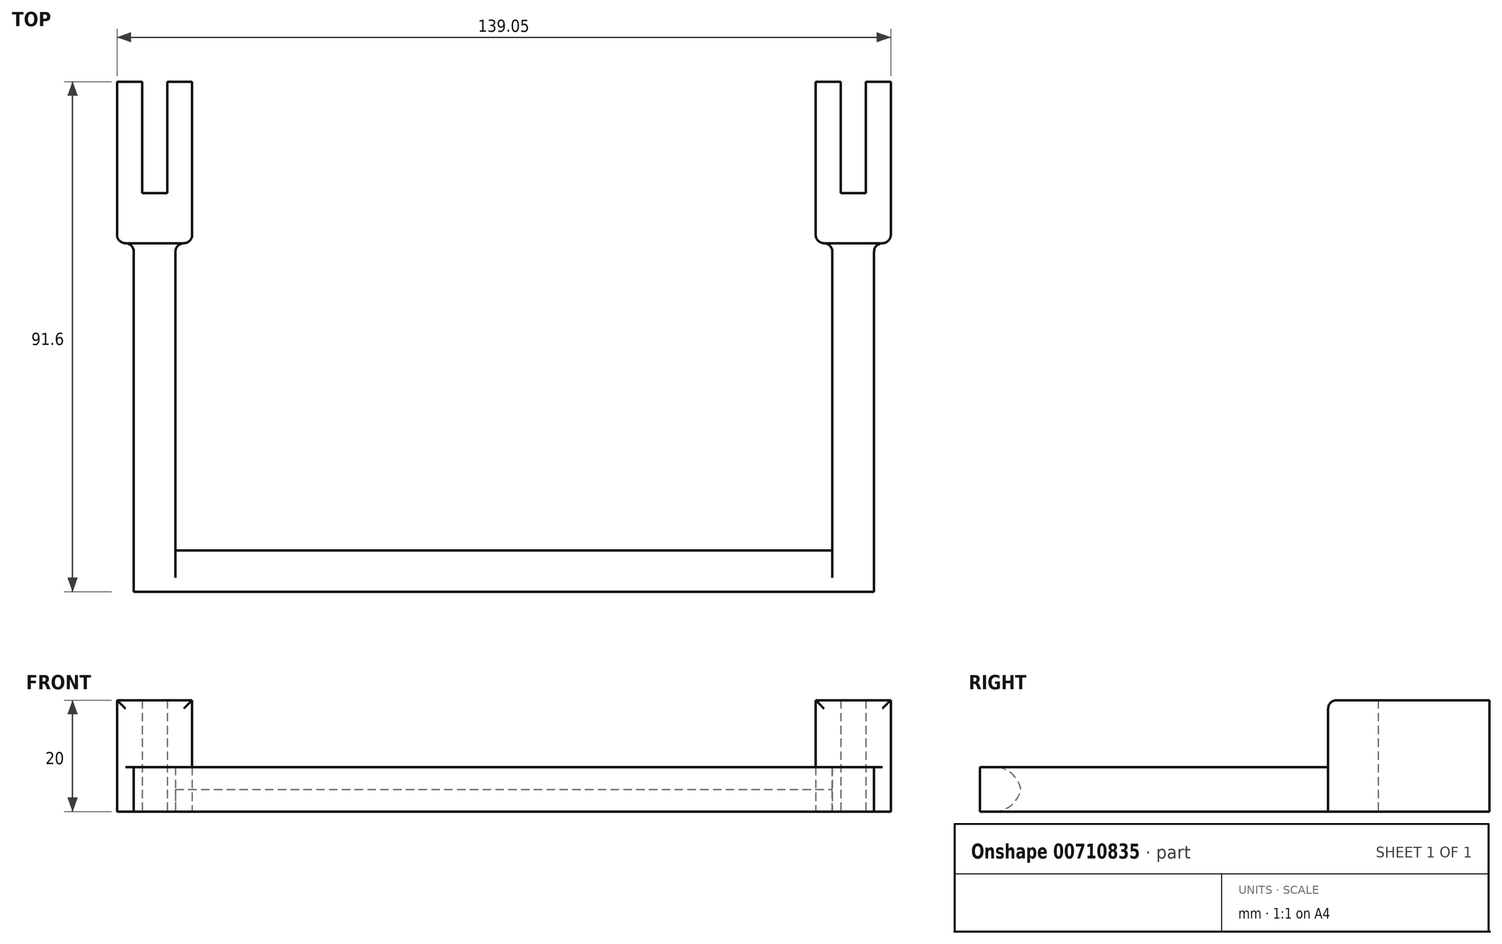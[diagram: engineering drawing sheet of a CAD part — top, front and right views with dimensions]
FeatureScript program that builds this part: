
annotation { "Feature Type Name" : "Feature", "Feature Type Description" : "" }
export const myFeature = defineFeature(function(context is Context, id is Id, definition is map)
    precondition{}
    {
        {
            var Q0;
            Q0=qCreatedBy(makeId("Top.planeOp"),FACE);
            var sketch = newSketch(context, id + "F0", { "sketchPlane" : qUnion([Q0])});
            skLineSegment(sketch, "E0", {"start": v(-132.3, 0) * mm, "end": v(-132.3, -29) * mm});
            skLineSegment(sketch, "E1", {"start": v(-132.3, -29) * mm, "end": v(-129.3, -29) * mm});
            skLineSegment(sketch, "E2", {"start": v(-129.3, -29) * mm, "end": v(-129.3, -91.6) * mm});
            skLineSegment(sketch, "E3", {"start": v(-129.3, -91.6) * mm, "end": v(3.75, -91.6) * mm});
            skLineSegment(sketch, "E4", {"start": v(3.75, -91.6) * mm, "end": v(3.75, -29) * mm});
            skLineSegment(sketch, "E5", {"start": v(-3.75, -29) * mm, "end": v(-3.75, -84.1) * mm});
            skLineSegment(sketch, "E6", {"start": v(-3.75, -84.1) * mm, "end": v(-121.8, -84.1) * mm});
            skLineSegment(sketch, "E7", {"start": v(-121.8, -84.1) * mm, "end": v(-121.8, -29) * mm});
            skLineSegment(sketch, "E8", {"start": v(-121.8, -29) * mm, "end": v(-118.8, -29) * mm});
            skLineSegment(sketch, "E9", {"start": v(-118.8, -29) * mm, "end": v(-118.8, 0) * mm});
            skLineSegment(sketch, "E10", {"start": v(-118.8, 0) * mm, "end": v(-123.3, 0) * mm});
            skLineSegment(sketch, "E11", {"start": v(-123.3, 0) * mm, "end": v(-123.3, -20) * mm});
            skLineSegment(sketch, "E12", {"start": v(-123.3, -20) * mm, "end": v(-127.8, -20) * mm});
            skLineSegment(sketch, "E13", {"start": v(-127.8, -20) * mm, "end": v(-127.8, 0) * mm});
            skLineSegment(sketch, "E14", {"start": v(-127.8, 0) * mm, "end": v(-132.3, 0) * mm});
            skLineSegment(sketch, "E15", {"start": v(3.75, -29) * mm, "end": v(6.75, -29) * mm});
            skLineSegment(sketch, "E16", {"start": v(6.75, -29) * mm, "end": v(6.75, 0) * mm});
            skLineSegment(sketch, "E17", {"start": v(6.75, 0) * mm, "end": v(2.25, 0) * mm});
            skLineSegment(sketch, "E18", {"start": v(2.25, 0) * mm, "end": v(2.25, -20) * mm});
            skLineSegment(sketch, "E19", {"start": v(2.25, -20) * mm, "end": v(-2.25, -20) * mm});
            skLineSegment(sketch, "E20", {"start": v(-2.25, -20) * mm, "end": v(-2.25, 0) * mm});
            skLineSegment(sketch, "E21", {"start": v(-2.25, 0) * mm, "end": v(-6.75, 0) * mm});
            skLineSegment(sketch, "E22", {"start": v(-6.75, 0) * mm, "end": v(-6.75, -29) * mm});
            skLineSegment(sketch, "E23", {"start": v(-6.75, -29) * mm, "end": v(-3.75, -29) * mm});
            skLineSegment(sketch, "E24", {"start": v(-125.55, -44.81) * mm, "end": v(-125.55, -20.56) * mm, "construction": true});
            skLineSegment(sketch, "E25", {"start": v(0, -53.1) * mm, "end": v(0, -35.47) * mm, "construction": true});
            skSolve(sketch);
        }
        {
            var Q0;
            Q0 = qSketchRegion(id + "F0", true);
            extrude(context, id + "F1", {"entities" : qUnion([Q0]), "depth" : 8 * mm, "offsetDistance" : 25 * mm});
        }
        {
            var Q0;
            Q0=makeQuery(id+"F1.opExtrude","CAP_FACE",FACE,{"disambiguationData":[OSD([sQuery(id+"F0.wireOp",EDGE,"E0"),sQuery(id+"F0.wireOp",EDGE,"E1"),sQuery(id+"F0.wireOp",EDGE,"E2"),sQuery(id+"F0.wireOp",EDGE,"E3"),sQuery(id+"F0.wireOp",EDGE,"E4"),sQuery(id+"F0.wireOp",EDGE,"E5"),sQuery(id+"F0.wireOp",EDGE,"E6"),sQuery(id+"F0.wireOp",EDGE,"E7"),sQuery(id+"F0.wireOp",EDGE,"E8"),sQuery(id+"F0.wireOp",EDGE,"E9"),sQuery(id+"F0.wireOp",EDGE,"E10"),sQuery(id+"F0.wireOp",EDGE,"E11"),sQuery(id+"F0.wireOp",EDGE,"E12"),sQuery(id+"F0.wireOp",EDGE,"E13"),sQuery(id+"F0.wireOp",EDGE,"E14"),sQuery(id+"F0.wireOp",EDGE,"E15"),sQuery(id+"F0.wireOp",EDGE,"E16"),sQuery(id+"F0.wireOp",EDGE,"E17"),sQuery(id+"F0.wireOp",EDGE,"E18"),sQuery(id+"F0.wireOp",EDGE,"E19"),sQuery(id+"F0.wireOp",EDGE,"E20"),sQuery(id+"F0.wireOp",EDGE,"E21"),sQuery(id+"F0.wireOp",EDGE,"E22"),sQuery(id+"F0.wireOp",EDGE,"E23")])],"isStart":false});
            var sketch = newSketch(context, id + "F2", { "sketchPlane" : qUnion([Q0])});
            skLineSegment(sketch, "E26", {"start": v(-132.3, 0) * mm, "end": v(-127.8, 0) * mm});
            skLineSegment(sketch, "E27", {"start": v(-127.8, 0) * mm, "end": v(-127.8, -20) * mm});
            skLineSegment(sketch, "E28", {"start": v(-127.8, -20) * mm, "end": v(-123.3, -20) * mm});
            skLineSegment(sketch, "E29", {"start": v(-123.3, -20) * mm, "end": v(-123.3, 0) * mm});
            skLineSegment(sketch, "E30", {"start": v(-123.3, 0) * mm, "end": v(-118.8, 0) * mm});
            skLineSegment(sketch, "E31", {"start": v(-118.8, 0) * mm, "end": v(-118.8, -29) * mm});
            skLineSegment(sketch, "E32", {"start": v(-118.8, -29) * mm, "end": v(-132.3, -29) * mm});
            skLineSegment(sketch, "E33", {"start": v(-132.3, -29) * mm, "end": v(-132.3, 0) * mm});
            skLineSegment(sketch, "E34", {"start": v(-6.75, 0) * mm, "end": v(-6.75, -29) * mm});
            skLineSegment(sketch, "E35", {"start": v(-6.75, -29) * mm, "end": v(6.75, -29) * mm});
            skLineSegment(sketch, "E36", {"start": v(6.75, -29) * mm, "end": v(6.75, 0) * mm});
            skLineSegment(sketch, "E37", {"start": v(6.75, 0) * mm, "end": v(2.25, 0) * mm});
            skLineSegment(sketch, "E38", {"start": v(2.25, 0) * mm, "end": v(2.25, -20) * mm});
            skLineSegment(sketch, "E39", {"start": v(2.25, -20) * mm, "end": v(-2.25, -20) * mm});
            skLineSegment(sketch, "E40", {"start": v(-2.25, -20) * mm, "end": v(-2.25, 0) * mm});
            skLineSegment(sketch, "E41", {"start": v(-2.25, 0) * mm, "end": v(-6.75, 0) * mm});
            skSolve(sketch);
        }
        {
            var Q0;
            Q0 = qSketchRegion(id + "F2", true);
            extrude(context, id + "F3", {"entities" : qUnion([Q0]), "operationType" : NewBodyOperationType.ADD, "depth" : (20 - 8) * mm, "offsetDistance" : 25 * mm});
        }
        {
            var Q0;
            Q0=makeQuery(id+"F1.opExtrude","SWEPT_EDGE",EDGE,{"disambiguationData":[OSD([sQuery(id+"F0.wireOp",EDGE,"E1"),sQuery(id+"F0.wireOp",EDGE,"E2")])]});
            var Q1;
            Q1=makeQuery(id+"F3.opExtrude","CAP_EDGE",EDGE,{"disambiguationData":[OSD([sQuery(id+"F2.wireOp",EDGE,"E32")])],"isStart":true});
            var Q2;
            Q2=makeQuery(id+"F1.opExtrude","SWEPT_EDGE",EDGE,{"disambiguationData":[OSD([sQuery(id+"F0.wireOp",EDGE,"E7"),sQuery(id+"F0.wireOp",EDGE,"E8")])]});
            var Q3;
            Q3=makeQuery(id+"F1.opExtrude","SWEPT_EDGE",EDGE,{"disambiguationData":[OSD([sQuery(id+"F0.wireOp",EDGE,"E5"),sQuery(id+"F0.wireOp",EDGE,"E23")])]});
            var Q4;
            Q4=makeQuery(id+"F3.opExtrude","CAP_EDGE",EDGE,{"disambiguationData":[OSD([sQuery(id+"F2.wireOp",EDGE,"E35")])],"isStart":true});
            var Q5;
            Q5=makeQuery(id+"F1.opExtrude","SWEPT_EDGE",EDGE,{"disambiguationData":[OSD([sQuery(id+"F0.wireOp",EDGE,"E4"),sQuery(id+"F0.wireOp",EDGE,"E15")])]});
            fillet(context, id + "F4", {"entities" : qUnion([Q0, Q1, Q2, Q3, Q4, Q5]), "radius" : 1.5 * mm, "tangentPropagation" : true, "allowEdgeOverflow" : false});
        }
        {
            var Q0;
            Q0=makeQuery(id+"F3.boolean.opBoolean","MERGE",EDGE,{"derivedFrom":[makeQuery(id+"F1.opExtrude","SWEPT_EDGE",EDGE,{"disambiguationData":[OSD([sQuery(id+"F0.wireOp",EDGE,"E0"),sQuery(id+"F0.wireOp",EDGE,"E1")])]}),makeQuery(id+"F3.opExtrude","SWEPT_EDGE",EDGE,{"disambiguationData":[OSD([sQuery(id+"F2.wireOp",EDGE,"E32"),sQuery(id+"F2.wireOp",EDGE,"E33")])]})]});
            var Q1;
            Q1=makeQuery(id+"F3.opExtrude","CAP_EDGE",EDGE,{"disambiguationData":[OSD([sQuery(id+"F2.wireOp",EDGE,"E32")])],"isStart":false});
            var Q2;
            Q2=makeQuery(id+"F3.boolean.opBoolean","MERGE",EDGE,{"derivedFrom":[makeQuery(id+"F1.opExtrude","SWEPT_EDGE",EDGE,{"disambiguationData":[OSD([sQuery(id+"F0.wireOp",EDGE,"E8"),sQuery(id+"F0.wireOp",EDGE,"E9")])]}),makeQuery(id+"F3.opExtrude","SWEPT_EDGE",EDGE,{"disambiguationData":[OSD([sQuery(id+"F2.wireOp",EDGE,"E31"),sQuery(id+"F2.wireOp",EDGE,"E32")])]})]});
            var Q3;
            Q3=makeQuery(id+"F3.boolean.opBoolean","MERGE",EDGE,{"derivedFrom":[makeQuery(id+"F1.opExtrude","SWEPT_EDGE",EDGE,{"disambiguationData":[OSD([sQuery(id+"F0.wireOp",EDGE,"E15"),sQuery(id+"F0.wireOp",EDGE,"E16")])]}),makeQuery(id+"F3.opExtrude","SWEPT_EDGE",EDGE,{"disambiguationData":[OSD([sQuery(id+"F2.wireOp",EDGE,"E35"),sQuery(id+"F2.wireOp",EDGE,"E36")])]})]});
            var Q4;
            Q4=makeQuery(id+"F3.opExtrude","CAP_EDGE",EDGE,{"disambiguationData":[OSD([sQuery(id+"F2.wireOp",EDGE,"E35")])],"isStart":false});
            var Q5;
            Q5=makeQuery(id+"F3.boolean.opBoolean","MERGE",EDGE,{"derivedFrom":[makeQuery(id+"F1.opExtrude","SWEPT_EDGE",EDGE,{"disambiguationData":[OSD([sQuery(id+"F0.wireOp",EDGE,"E22"),sQuery(id+"F0.wireOp",EDGE,"E23")])]}),makeQuery(id+"F3.opExtrude","SWEPT_EDGE",EDGE,{"disambiguationData":[OSD([sQuery(id+"F2.wireOp",EDGE,"E34"),sQuery(id+"F2.wireOp",EDGE,"E35")])]})]});
            fillet(context, id + "F5", {"entities" : qUnion([Q0, Q1, Q2, Q3, Q4, Q5]), "radius" : 1.5 * mm, "tangentPropagation" : true, "allowEdgeOverflow" : false});
        }
        {
            var Q0;
            Q0=makeQuery(id+"F1.opExtrude","CAP_EDGE",EDGE,{"disambiguationData":[OSD([sQuery(id+"F0.wireOp",EDGE,"E6")])],"isStart":false});
            var Q1;
            Q1=makeQuery(id+"F1.opExtrude","CAP_EDGE",EDGE,{"disambiguationData":[OSD([sQuery(id+"F0.wireOp",EDGE,"E6")])],"isStart":true});
            fillet(context, id + "F6", {"entities" : qUnion([Q0, Q1]), "radius" : 5 * mm, "tangentPropagation" : true, "allowEdgeOverflow" : false});
        }
    });
